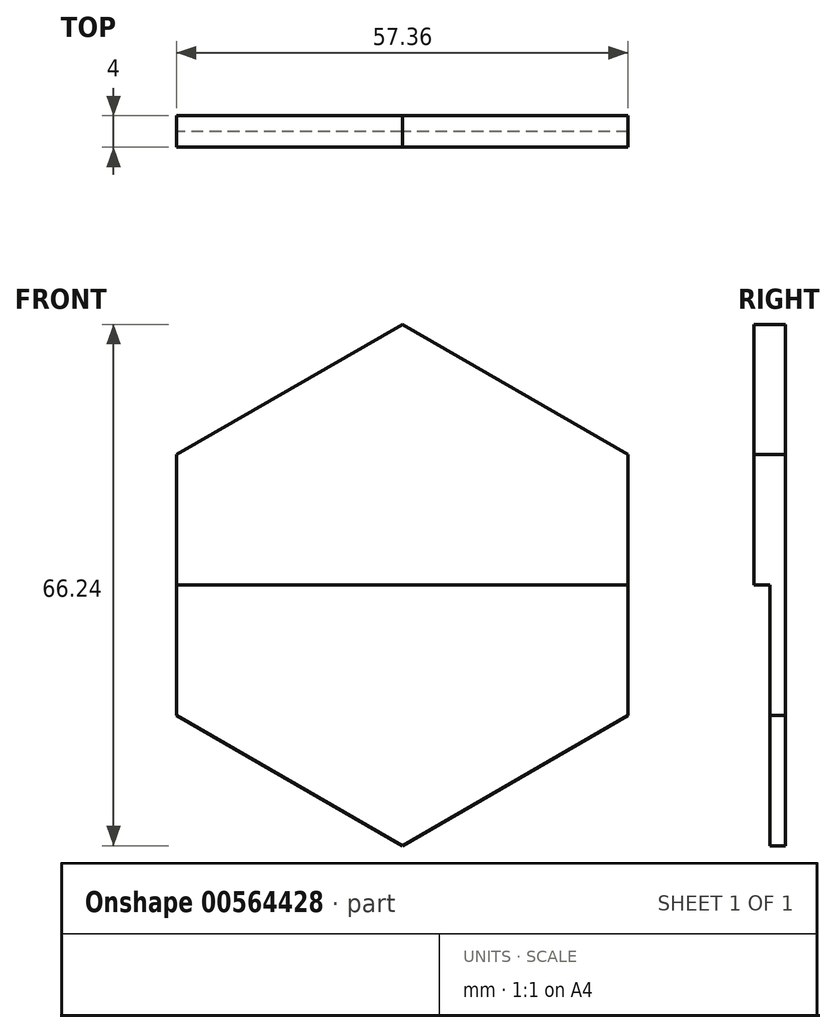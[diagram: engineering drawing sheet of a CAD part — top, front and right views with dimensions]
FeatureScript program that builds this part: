
annotation { "Feature Type Name" : "Feature", "Feature Type Description" : "" }
export const myFeature = defineFeature(function(context is Context, id is Id, definition is map)
    precondition{}
    {
        {
            var Q0;
            Q0=qCreatedBy(makeId("Front.planeOp"),FACE);
            var sketch = newSketch(context, id + "F0", { "sketchPlane" : qUnion([Q0])});
            skCircle(sketch, "E0.cCircle", {"center": v(0, 0) * mm, "radius": 28.68 * mm, "construction": true});
            skLineSegment(sketch, "E0.0", {"start": v(-28.68, -16.56) * mm, "end": v(-28.68, 16.56) * mm});
            skLineSegment(sketch, "E0.1", {"start": v(-28.68, 16.56) * mm, "end": v(0, 33.12) * mm});
            skLineSegment(sketch, "E0.2", {"start": v(0, 33.12) * mm, "end": v(28.68, 16.56) * mm});
            skLineSegment(sketch, "E0.3", {"start": v(28.68, 16.56) * mm, "end": v(28.68, -16.56) * mm});
            skLineSegment(sketch, "E0.4", {"start": v(28.68, -16.56) * mm, "end": v(0, -33.12) * mm});
            skLineSegment(sketch, "E0.5", {"start": v(0, -33.12) * mm, "end": v(-28.68, -16.56) * mm});
            skPoint(sketch, "E0.0.midPoint", {"position": v(-28.68, 0) * mm});
            skLineSegment(sketch, "E1", {"start": v(-28.68, 0) * mm, "end": v(28.68, 0) * mm});
            skSolve(sketch);
        }
        {
            var Q0;
            {var subQ3=sQuery(id+"F0.wireOp",EDGE,"E0.1");Q0=makeQuery(id+"F0.imprint","IMPRINT",FACE,{"disambiguationData":[TD([[makeQuery(id+"F0.imprint","IMPRINT",EDGE,{"derivedFrom":subQ3}),-1.0]])]});}
            extrude(context, id + "F1", {"entities" : qUnion([Q0]), "depth" : 4 * mm, "offsetDistance" : 25 * mm});
        }
        {
            var Q0;
            {var subQ1=sQuery(id+"F0.wireOp",EDGE,"E0.4");Q0=makeQuery(id+"F0.imprint","IMPRINT",FACE,{"disambiguationData":[TD([[makeQuery(id+"F0.imprint","IMPRINT",EDGE,{"derivedFrom":subQ1}),-1.0]])]});}
            extrude(context, id + "F2", {"entities" : qUnion([Q0]), "operationType" : NewBodyOperationType.ADD, "depth" : 2 * mm, "offsetDistance" : 25 * mm});
        }
    });
